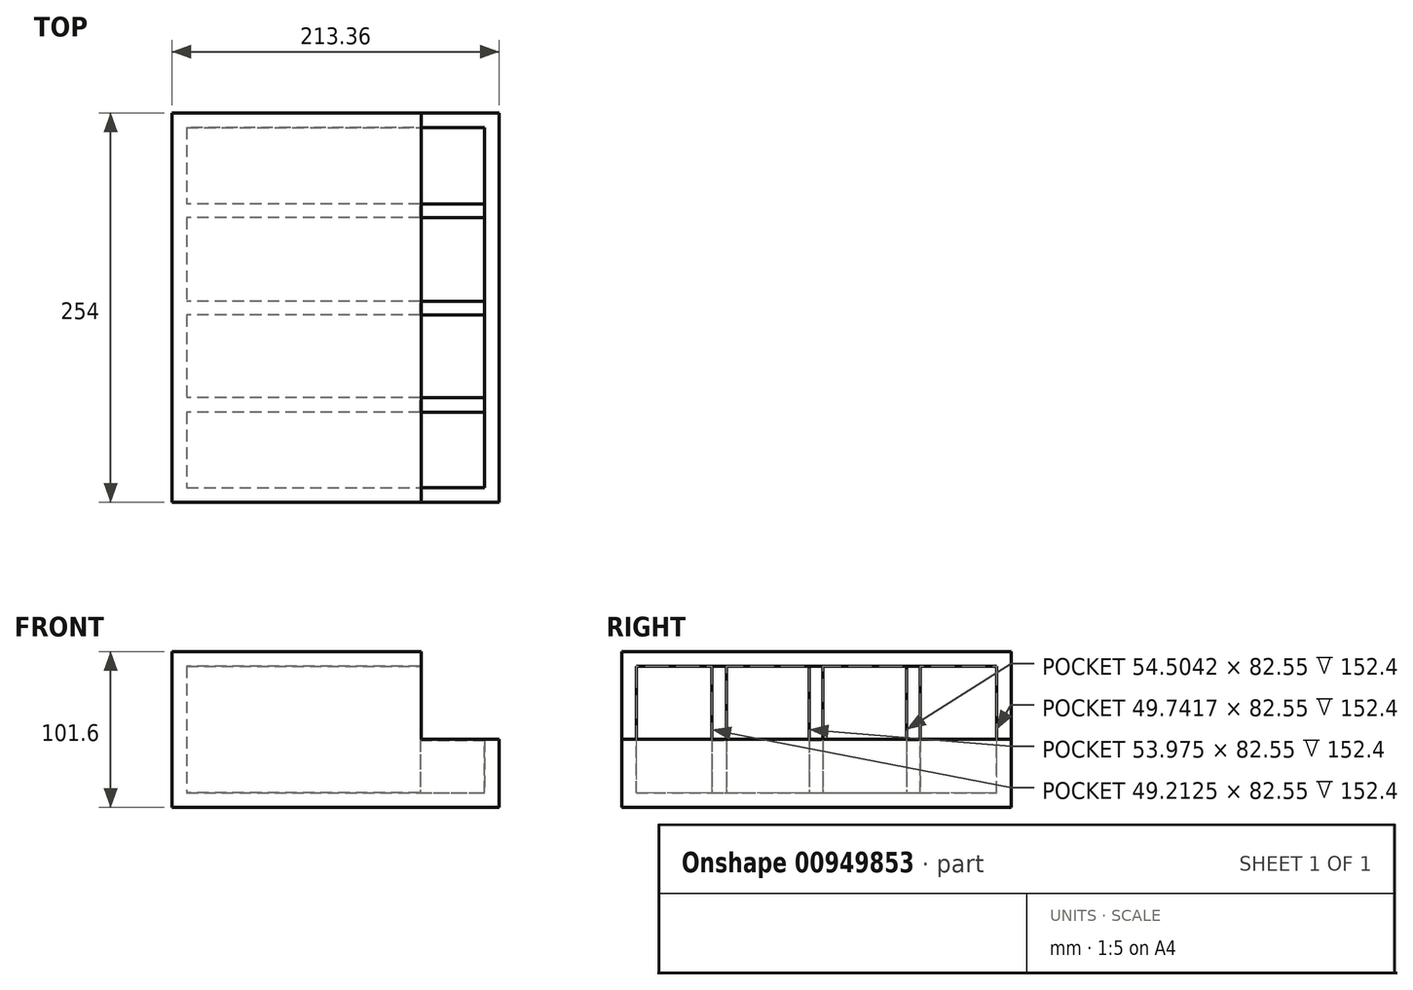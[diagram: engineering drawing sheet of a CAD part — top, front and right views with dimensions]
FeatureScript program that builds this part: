
annotation { "Feature Type Name" : "Feature", "Feature Type Description" : "" }
export const myFeature = defineFeature(function(context is Context, id is Id, definition is map)
    precondition{}
    {
        {
            var Q0;
            Q0=qCreatedBy(makeId("Front.planeOp"),FACE);
            var sketch = newSketch(context, id + "F0", { "sketchPlane" : qUnion([Q0])});
            skLineSegment(sketch, "E0", {"start": v(-213.36, 57.15) * mm, "end": v(-213.36, -44.45) * mm});
            skLineSegment(sketch, "E1", {"start": v(-213.36, 57.15) * mm, "end": v(-50.8, 57.15) * mm});
            skLineSegment(sketch, "E2", {"start": v(-50.8, 0) * mm, "end": v(-50.8, 57.15) * mm});
            skLineSegment(sketch, "E3", {"start": v(0, 0) * mm, "end": v(-50.8, 0) * mm});
            skLineSegment(sketch, "E4", {"start": v(0, -44.45) * mm, "end": v(0, 0) * mm});
            skLineSegment(sketch, "E5", {"start": v(-213.36, -44.45) * mm, "end": v(0, -44.45) * mm});
            skSolve(sketch);
        }
        {
            var Q0;
            Q0=makeQuery(id+"F0.imprint","IMPRINT",FACE,{"disambiguationData":[TD([[makeQuery(id+"F0.imprint","IMPRINT",EDGE,{"derivedFrom":sQuery(id+"F0.wireOp",EDGE,"E0")}),1.0]])]});
            extrude(context, id + "F1", {"entities" : qUnion([Q0]), "depth" : 254 * mm, "offsetDistance" : 25.4 * mm});
        }
        {
            var Q0;
            Q0=makeQuery(id+"F1.opExtrude","SWEPT_FACE",FACE,{"disambiguationData":[OSD([sQuery(id+"F0.wireOp",EDGE,"E3")])]});
            var sketch = newSketch(context, id + "F2", { "sketchPlane" : qUnion([Q0])});
            skLineSegment(sketch, "E6", {"start": v(-50.8, -244.47) * mm, "end": v(-9.53, -244.47) * mm});
            skLineSegment(sketch, "E7", {"start": v(-9.53, -244.47) * mm, "end": v(-9.53, -9.52) * mm});
            skLineSegment(sketch, "E8", {"start": v(-50.8, -244.47) * mm, "end": v(-50.8, -254) * mm});
            skLineSegment(sketch, "E9", {"start": v(-9.53, -244.47) * mm, "end": v(0, -244.47) * mm, "construction": true});
            skLineSegment(sketch, "E10", {"start": v(-9.53, -9.52) * mm, "end": v(-50.8, -9.52) * mm});
            skLineSegment(sketch, "E11", {"start": v(-9.53, -9.52) * mm, "end": v(-9.53, 0) * mm, "construction": true});
            skSolve(sketch);
        }
        {
            var Q0;
            {var subQ0=sQuery(id+"F2.wireOp",EDGE,"E6");Q0=makeQuery(id+"F2.imprint","IMPRINT",FACE,{"disambiguationData":[TD([[makeQuery(id+"F2.imprint","IMPRINT",EDGE,{"derivedFrom":subQ0}),1.0]])]});}
            extrude(context, id + "F3", {"entities" : qUnion([Q0]), "operationType" : NewBodyOperationType.REMOVE, "depth" : -34.92 * mm, "offsetDistance" : 25.4 * mm});
        }
        {
            var Q0;
            {var subQ0=sQuery(id+"F0.wireOp",EDGE,"E2");Q0=makeQuery(id+"F3.boolean.opBoolean","MERGE",FACE,{"derivedFrom":[makeQuery(id+"F1.opExtrude","SWEPT_FACE",FACE,{"disambiguationData":[OSD([subQ0])]})],"fromTools":[makeQuery(id+"F3.opExtrude","SWEPT_FACE",FACE,{"disambiguationData":[OSD([subQ0,sQuery(id+"F0.wireOp",EDGE,"E3")])]})]});}
            var sketch = newSketch(context, id + "F4", { "sketchPlane" : qUnion([Q0])});
            skLineSegment(sketch, "E12", {"start": v(-244.47, 0) * mm, "end": v(-244.47, 47.62) * mm});
            skLineSegment(sketch, "E13", {"start": v(-9.52, 0) * mm, "end": v(-9.52, 47.62) * mm});
            skLineSegment(sketch, "E14", {"start": v(-9.53, 47.62) * mm, "end": v(-244.47, 47.62) * mm});
            skLineSegment(sketch, "E15", {"start": v(-254.05, 47.62) * mm, "end": v(-254.05, 57.15) * mm, "construction": true});
            skLineSegment(sketch, "E16", {"start": v(-254, 25.15) * mm, "end": v(-244.47, 25.15) * mm, "construction": true});
            skLineSegment(sketch, "E17", {"start": v(-9.53, 47.62) * mm, "end": v(0, 47.62) * mm, "construction": true});
            skLineSegment(sketch, "E18", {"start": v(-244.47, 0) * mm, "end": v(-244.47, -34.93) * mm});
            skLineSegment(sketch, "E19", {"start": v(-244.47, -34.93) * mm, "end": v(-9.52, -34.92) * mm});
            skLineSegment(sketch, "E20", {"start": v(-9.52, -34.93) * mm, "end": v(-9.52, 0) * mm});
            skSolve(sketch);
        }
        {
            var Q0;
            Q0=makeQuery(id+"F4.imprint","IMPRINT",FACE,{"disambiguationData":[TD([[makeQuery(id+"F4.imprint","IMPRINT",EDGE,{"derivedFrom":sQuery(id+"F4.wireOp",EDGE,"E12")}),-1.0]])]});
            extrude(context, id + "F5", {"entities" : qUnion([Q0]), "operationType" : NewBodyOperationType.REMOVE, "surfaceOperationType" : NewSurfaceOperationType.ADD, "oppositeDirection" : true, "depth" : 153.03 * mm, "offsetDistance" : 25.4 * mm});
        }
        {
            var Q0;
            Q0=makeQuery(id+"F5.boolean.opBoolean","COPY",FACE,{"derivedFrom":makeQuery(id+"F5.opExtrude","CAP_FACE",FACE,{"disambiguationData":[OSD([sQuery(id+"F4.wireOp",EDGE,"E12"),sQuery(id+"F4.wireOp",EDGE,"E13"),sQuery(id+"F4.wireOp",EDGE,"E14"),sQuery(id+"F4.wireOp",EDGE,"E18"),sQuery(id+"F4.wireOp",EDGE,"E19"),sQuery(id+"F4.wireOp",EDGE,"E20")])],"isStart":false})});
            var sketch = newSketch(context, id + "F6", { "sketchPlane" : qUnion([Q0])});
            skLineSegment(sketch, "E21", {"start": v(-190.5, 57.15) * mm, "end": v(-190.5, -44.45) * mm});
            skLineSegment(sketch, "E22", {"start": v(-127, 57.15) * mm, "end": v(-127, -44.45) * mm});
            skLineSegment(sketch, "E23", {"start": v(-63.5, 57.15) * mm, "end": v(-63.5, -44.45) * mm});
            skLineSegment(sketch, "E24", {"start": v(-254, 57.15) * mm, "end": v(-190.5, 57.15) * mm, "construction": true});
            skLineSegment(sketch, "E25", {"start": v(-190.5, 57.15) * mm, "end": v(-127, 57.15) * mm, "construction": true});
            skLineSegment(sketch, "E26", {"start": v(-127, 57.15) * mm, "end": v(-63.5, 57.15) * mm, "construction": true});
            skLineSegment(sketch, "E27", {"start": v(-195.26, 57.15) * mm, "end": v(-195.26, -44.45) * mm});
            skLineSegment(sketch, "E28", {"start": v(-185.74, 57.15) * mm, "end": v(-185.74, -44.45) * mm});
            skLineSegment(sketch, "E29", {"start": v(-195.26, 6.7) * mm, "end": v(-190.5, 6.7) * mm, "construction": true});
            skLineSegment(sketch, "E30", {"start": v(-195.26, 13.1) * mm, "end": v(-185.74, 13.1) * mm, "construction": true});
            skLineSegment(sketch, "E31", {"start": v(-131.76, 57.15) * mm, "end": v(-131.76, -44.45) * mm});
            skLineSegment(sketch, "E32", {"start": v(-131.76, 21.2) * mm, "end": v(-127, 21.2) * mm, "construction": true});
            skLineSegment(sketch, "E33", {"start": v(-121.44, 57.15) * mm, "end": v(-122.77, 57.15) * mm});
            skLineSegment(sketch, "E34", {"start": v(-122.77, 57.15) * mm, "end": v(-122.77, -44.9) * mm});
            skLineSegment(sketch, "E35", {"start": v(-127, 22.14) * mm, "end": v(-122.77, 22.14) * mm, "construction": true});
            skLineSegment(sketch, "E36", {"start": v(-68.26, 57.15) * mm, "end": v(-68.26, -44.45) * mm});
            skLineSegment(sketch, "E37", {"start": v(-59.27, -44.45) * mm, "end": v(-59.27, 57.15) * mm});
            skLineSegment(sketch, "E38", {"start": v(-68.26, 4.39) * mm, "end": v(-63.5, 4.39) * mm, "construction": true});
            skLineSegment(sketch, "E39", {"start": v(-59.27, 4.39) * mm, "end": v(-63.5, 4.39) * mm, "construction": true});
            skSolve(sketch);
        }
        {
            var Q0;
            {var subQ0=sQuery(id+"F6.wireOp",EDGE,"E22");var subQ1=makeQuery(id+"F5.boolean.opBoolean","COPY",EDGE,{"derivedFrom":makeQuery(id+"F5.opExtrude","CAP_EDGE",EDGE,{"disambiguationData":[OSD([sQuery(id+"F4.wireOp",EDGE,"E14")])],"isStart":false})});var subQ2=makeQuery(id+"F6.imprint","INTERSECT",VERTEX,{"derivedFrom":[subQ1,subQ0]});Q0=makeQuery(id+"F6.imprint","IMPRINT",FACE,{"disambiguationData":[TD([[makeQuery(id+"F6.imprint","IMPRINT",EDGE,{"disambiguationData":[TD([[subQ2,-1.0]])],"derivedFrom":subQ0}),1.0]])]});}
            var Q1;
            {var subQ0=sQuery(id+"F6.wireOp",EDGE,"E22");var subQ1=makeQuery(id+"F5.boolean.opBoolean","COPY",EDGE,{"derivedFrom":makeQuery(id+"F5.opExtrude","CAP_EDGE",EDGE,{"disambiguationData":[OSD([sQuery(id+"F4.wireOp",EDGE,"E14")])],"isStart":false})});var subQ2=makeQuery(id+"F6.imprint","INTERSECT",VERTEX,{"derivedFrom":[subQ1,subQ0]});Q1=makeQuery(id+"F6.imprint","IMPRINT",FACE,{"disambiguationData":[TD([[makeQuery(id+"F6.imprint","IMPRINT",EDGE,{"disambiguationData":[TD([[subQ2,-1.0]])],"derivedFrom":subQ0}),-1.0]])]});}
            var Q2;
            {var subQ0=sQuery(id+"F6.wireOp",EDGE,"E23");var subQ1=makeQuery(id+"F5.boolean.opBoolean","COPY",EDGE,{"derivedFrom":makeQuery(id+"F5.opExtrude","CAP_EDGE",EDGE,{"disambiguationData":[OSD([sQuery(id+"F4.wireOp",EDGE,"E14")])],"isStart":false})});var subQ2=makeQuery(id+"F6.imprint","INTERSECT",VERTEX,{"derivedFrom":[subQ1,subQ0]});Q2=makeQuery(id+"F6.imprint","IMPRINT",FACE,{"disambiguationData":[TD([[makeQuery(id+"F6.imprint","IMPRINT",EDGE,{"disambiguationData":[TD([[subQ2,-1.0]])],"derivedFrom":subQ0}),-1.0]])]});}
            var Q3;
            {var subQ0=sQuery(id+"F6.wireOp",EDGE,"E23");var subQ1=makeQuery(id+"F5.boolean.opBoolean","COPY",EDGE,{"derivedFrom":makeQuery(id+"F5.opExtrude","CAP_EDGE",EDGE,{"disambiguationData":[OSD([sQuery(id+"F4.wireOp",EDGE,"E14")])],"isStart":false})});var subQ2=makeQuery(id+"F6.imprint","INTERSECT",VERTEX,{"derivedFrom":[subQ1,subQ0]});Q3=makeQuery(id+"F6.imprint","IMPRINT",FACE,{"disambiguationData":[TD([[makeQuery(id+"F6.imprint","IMPRINT",EDGE,{"disambiguationData":[TD([[subQ2,-1.0]])],"derivedFrom":subQ0}),1.0]])]});}
            var Q4;
            {var subQ0=sQuery(id+"F6.wireOp",EDGE,"E21");var subQ1=makeQuery(id+"F5.boolean.opBoolean","COPY",EDGE,{"derivedFrom":makeQuery(id+"F5.opExtrude","CAP_EDGE",EDGE,{"disambiguationData":[OSD([sQuery(id+"F4.wireOp",EDGE,"E14")])],"isStart":false})});var subQ2=makeQuery(id+"F6.imprint","INTERSECT",VERTEX,{"derivedFrom":[subQ1,subQ0]});Q4=makeQuery(id+"F6.imprint","IMPRINT",FACE,{"disambiguationData":[TD([[makeQuery(id+"F6.imprint","IMPRINT",EDGE,{"disambiguationData":[TD([[subQ2,-1.0]])],"derivedFrom":subQ0}),-1.0]])]});}
            var Q5;
            {var subQ0=sQuery(id+"F6.wireOp",EDGE,"E21");var subQ1=makeQuery(id+"F5.boolean.opBoolean","COPY",EDGE,{"derivedFrom":makeQuery(id+"F5.opExtrude","CAP_EDGE",EDGE,{"disambiguationData":[OSD([sQuery(id+"F4.wireOp",EDGE,"E14")])],"isStart":false})});var subQ2=makeQuery(id+"F6.imprint","INTERSECT",VERTEX,{"derivedFrom":[subQ1,subQ0]});Q5=makeQuery(id+"F6.imprint","IMPRINT",FACE,{"disambiguationData":[TD([[makeQuery(id+"F6.imprint","IMPRINT",EDGE,{"disambiguationData":[TD([[subQ2,-1.0]])],"derivedFrom":subQ0}),1.0]])]});}
            extrude(context, id + "F7", {"entities" : qUnion([Q0, Q1, Q2, Q3, Q4, Q5]), "operationType" : NewBodyOperationType.ADD, "depth" : 152.4 * mm, "offsetDistance" : 25.4 * mm});
        }
        {
            var Q0;
            Q0=makeQuery(id+"F5.boolean.opBoolean","MERGE",FACE,{"derivedFrom":[makeQuery(id+"F3.boolean.opBoolean","COPY",FACE,{"derivedFrom":makeQuery(id+"F3.opExtrude","CAP_FACE",FACE,{"disambiguationData":[OSD([sQuery(id+"F0.wireOp",EDGE,"E2"),sQuery(id+"F0.wireOp",EDGE,"E3"),sQuery(id+"F2.wireOp",EDGE,"E6"),sQuery(id+"F2.wireOp",EDGE,"E7"),sQuery(id+"F2.wireOp",EDGE,"E10")])],"isStart":false})})],"fromTools":[makeQuery(id+"F5.opExtrude","SWEPT_FACE",FACE,{"disambiguationData":[OSD([sQuery(id+"F4.wireOp",EDGE,"E19")])]})]});
            var sketch = newSketch(context, id + "F8", { "sketchPlane" : qUnion([Q0])});
            skLineSegment(sketch, "E40", {"start": v(-51.44, -68.26) * mm, "end": v(-9.53, -68.26) * mm});
            skLineSegment(sketch, "E41", {"start": v(-51.44, -122.77) * mm, "end": v(-9.53, -122.77) * mm});
            skLineSegment(sketch, "E42", {"start": v(-51.44, -131.76) * mm, "end": v(-9.53, -131.76) * mm});
            skLineSegment(sketch, "E43", {"start": v(-51.44, -185.74) * mm, "end": v(-9.53, -185.74) * mm});
            skLineSegment(sketch, "E44", {"start": v(-51.44, -195.26) * mm, "end": v(-9.53, -195.26) * mm});
            skLineSegment(sketch, "E45", {"start": v(-51.44, -59.27) * mm, "end": v(-9.53, -59.27) * mm});
            skSolve(sketch);
        }
        {
            var Q0;
            {var subQ0=sQuery(id+"F8.wireOp",EDGE,"E40");Q0=makeQuery(id+"F8.imprint","IMPRINT",FACE,{"disambiguationData":[TD([[makeQuery(id+"F8.imprint","IMPRINT",EDGE,{"derivedFrom":subQ0}),1.0]])]});}
            var Q1;
            {var subQ0=sQuery(id+"F8.wireOp",EDGE,"E41");Q1=makeQuery(id+"F8.imprint","IMPRINT",FACE,{"disambiguationData":[TD([[makeQuery(id+"F8.imprint","IMPRINT",EDGE,{"derivedFrom":subQ0}),-1.0]])]});}
            var Q2;
            {var subQ0=sQuery(id+"F8.wireOp",EDGE,"E43");Q2=makeQuery(id+"F8.imprint","IMPRINT",FACE,{"disambiguationData":[TD([[makeQuery(id+"F8.imprint","IMPRINT",EDGE,{"derivedFrom":subQ0}),-1.0]])]});}
            extrude(context, id + "F9", {"entities" : qUnion([Q0, Q1, Q2]), "depth" : 34.3 * mm, "offsetDistance" : 25.4 * mm});
        }
    });
